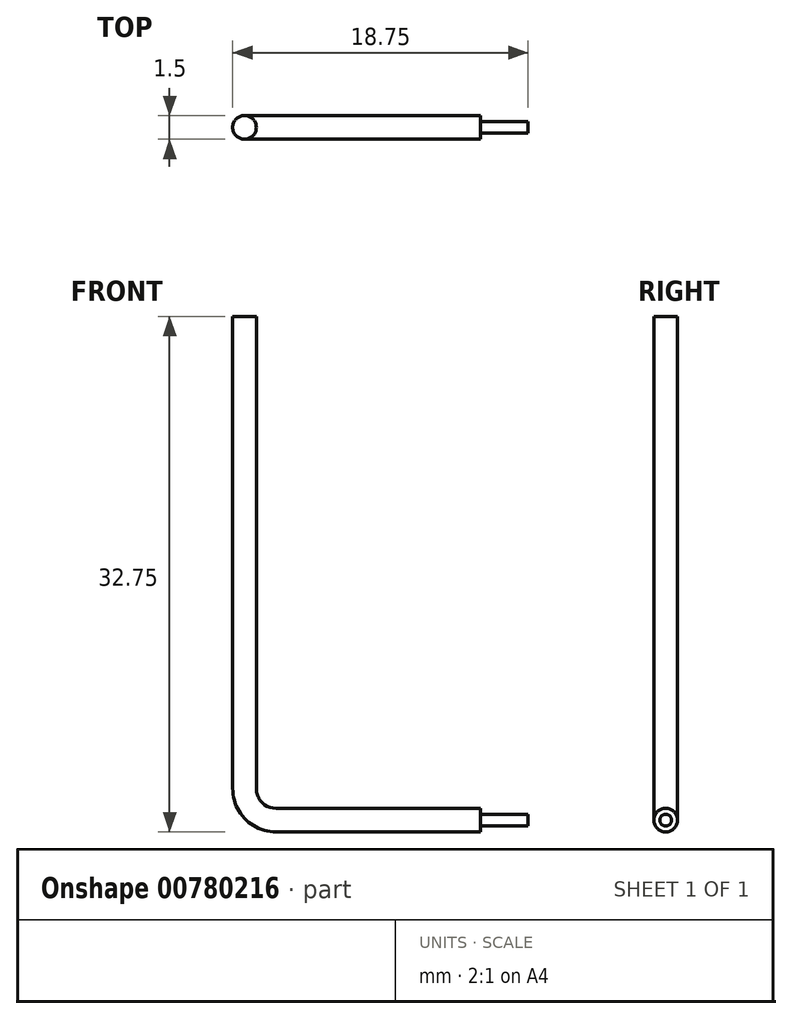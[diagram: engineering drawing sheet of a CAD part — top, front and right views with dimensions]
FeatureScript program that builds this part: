
annotation { "Feature Type Name" : "Feature", "Feature Type Description" : "" }
export const myFeature = defineFeature(function(context is Context, id is Id, definition is map)
    precondition{}
    {
        {
            var Q0;
            Q0=qCreatedBy(makeId("Front.planeOp"),FACE);
            var sketch = newSketch(context, id + "F0", { "sketchPlane" : qUnion([Q0])});
            skLineSegment(sketch, "E0", {"start": v(0, 2) * mm, "end": v(0, 30) * mm});
            skLineSegment(sketch, "E1", {"start": v(2, 0) * mm, "end": v(15, 0) * mm});
            skPoint(sketch, "E2.visualSharp", {"position": v(0, 32) * mm});
            skPoint(sketch, "E3.visualSharp", {"position": v(0, 0) * mm});
            skArc(sketch, "E3.filletArc", {"start": v(0, 2) * mm, "mid": v(0.59, 0.59) * mm, "end": v(2, 0) * mm});
            skLineSegment(sketch, "E4", {"start": v(0, 30) * mm, "end": v(0, 32) * mm});
            skSolve(sketch);
        }
        {
            var Q0;
            Q0=qCreatedBy(makeId("Right.planeOp"),FACE);
            cPlane(context, id + "F1", {"entities" : qUnion([Q0]), "cplaneType" : CPlaneType.OFFSET, "offset" : 15 * mm, "width" : 150 * mm, "height" : 150 * mm});
        }
        {
            var Q0;
            Q0=qCreatedBy(id+"F1.planeOp",FACE);
            var sketch = newSketch(context, id + "F2", { "sketchPlane" : qUnion([Q0])});
            skCircle(sketch, "E5", {"center": v(0, 0) * mm, "radius": 0.38 * mm});
            skCircle(sketch, "E6", {"center": v(0, 0) * mm, "radius": 0.75 * mm});
            skSolve(sketch);
        }
        {
            var Q0;
            Q0=qSketchRegion(id+"F2",true);
            var Q1;
            Q1=makeQuery(id+"F2.imprint","IMPRINT",FACE,{"disambiguationData":[TD([[makeQuery(id+"F2.imprint","IMPRINT",EDGE,{"derivedFrom":sQuery(id+"F2.wireOp",EDGE,"E5")}),1.0]])]});
            var Q2;
            Q2=sQuery(id+"F0.wireOp",EDGE,"E1");
            var Q3;
            Q3=sQuery(id+"F0.wireOp",EDGE,"E3.filletArc");
            var Q4;
            Q4=sQuery(id+"F0.wireOp",EDGE,"E0");
            var Q5;
            Q5=sQuery(id+"F0.wireOp",EDGE,"E2.filletArc");
            var Q6;
            Q6=sQuery(id+"F0.wireOp",EDGE,"E4");
            sweep(context, id + "F3", {"profiles" : qUnion([Q0, Q1]), "path" : qUnion([Q2, Q3, Q4, Q5, Q6])});
        }
        {
            var Q0;
            Q0=makeQuery(id+"F2.imprint","IMPRINT",FACE,{"disambiguationData":[TD([[makeQuery(id+"F2.imprint","IMPRINT",EDGE,{"derivedFrom":sQuery(id+"F2.wireOp",EDGE,"E5")}),1.0]])]});
            extrude(context, id + "F4", {"entities" : qUnion([Q0]), "operationType" : NewBodyOperationType.ADD, "depth" : 3 * mm, "offsetDistance" : 25 * mm});
        }
    });
